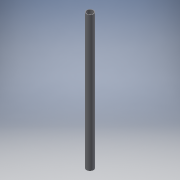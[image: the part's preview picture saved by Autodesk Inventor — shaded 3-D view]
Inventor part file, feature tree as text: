
AUTODESK INVENTOR PART (.ipt)
format: ipt  version: 2018.2 (Build 222227000, 227)  size: 93,184 bytes
history: native  units: mm
features: other x1, extrude x1, sketch x1
ambient origin geometry x8: Origin, YZ Plane, XZ Plane, XY Plane, X Axis, Y Axis, Z Axis, Center Point
bodies: Body1 (feature_tree)
feature tree (3):
  other  "ソリッド1"
  extrude  "押し出し1"  Depth=16.0mm
  sketch  "スケッチ1"
